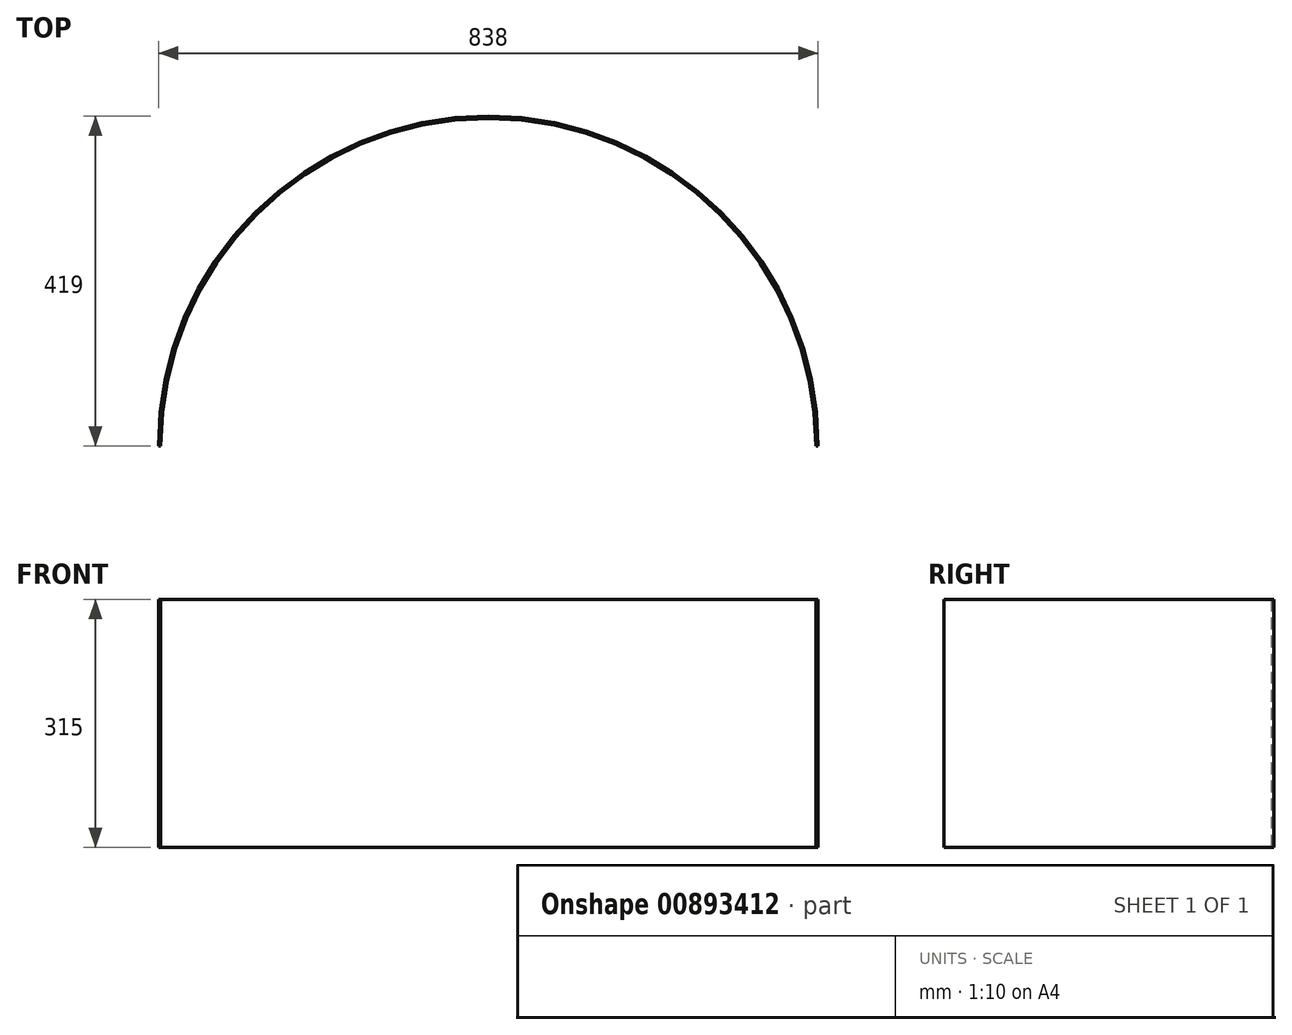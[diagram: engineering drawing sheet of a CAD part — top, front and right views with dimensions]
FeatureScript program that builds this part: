
annotation { "Feature Type Name" : "Feature", "Feature Type Description" : "" }
export const myFeature = defineFeature(function(context is Context, id is Id, definition is map)
    precondition{}
    {
        {
            var Q0;
            Q0=qCreatedBy(makeId("Top.planeOp"),FACE);
            var sketch = newSketch(context, id + "F0", { "sketchPlane" : qUnion([Q0])});
            skArc(sketch, "E0", {"start": v(419, 0) * mm, "mid": v(0, 419) * mm, "end": v(-419, 0) * mm});
            skArc(sketch, "E1", {"start": v(416, 0) * mm, "mid": v(0, 416) * mm, "end": v(-416, 0) * mm});
            skLineSegment(sketch, "E2", {"start": v(416, 0) * mm, "end": v(419, 0) * mm});
            skLineSegment(sketch, "E3", {"start": v(-416, 0) * mm, "end": v(-419, 0) * mm});
            skSolve(sketch);
        }
        {
            var Q0;
            Q0 = qSketchRegion(id + "F0", true);
            extrude(context, id + "F1", {"entities" : qUnion([Q0]), "depth" : 315 * mm, "offsetDistance" : 25 * mm});
        }
    });
